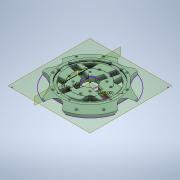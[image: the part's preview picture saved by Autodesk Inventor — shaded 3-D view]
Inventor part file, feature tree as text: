
AUTODESK INVENTOR PART (.ipt)
format: ipt  version: 2020 (Build 240168000, 168)  size: 684,032 bytes
history: native  units: mm
features: extrude x12, sketch x11, projected_geometry x8, other x6, pattern_circular x3, revolve x1, hole x1
ambient origin geometry x8: Origin, YZ Plane, XZ Plane, XY Plane, X Axis, Y Axis, Z Axis, Center Point
bodies: Body1 (feature_tree)
feature tree (42):
  other  "Твердое тело1"
  sketch  "Эскиз1"
  sketch  "Эскиз2"
  sketch  "Эскиз3"
  other  "РабОсь1"
  revolve  "Вращение1"
  hole  "Отверстие1"  [1 undecoded]
  other  "РабПлоскость1"
  other  "РабПлоскость2"
  extrude  "Выдавливание2"  Depth=44.0mm
  pattern_circular  "Круговой массив1"  Count=4 Angle=360.0deg
  other  "РабПлоскость3"
  extrude  "Выдавливание6"  Depth=7.0mm
  extrude  "Выдавливание7"  Depth=13.0mm
  pattern_circular  "Круговой массив2"  Angle=90.0deg  [1 undecoded]
  extrude  "Выдавливание8"  [1 undecoded]
  pattern_circular  "Круговой массив3"  [2 undecoded]
  extrude  "Выдавливание9"  Depth=6.0mm
  extrude  "Выдавливание10"  Depth=6.0mm
  other  "РабПлоскость4"
  extrude  "Выдавливание11"  Depth=6.0mm
  extrude  "Выдавливание1"  Depth=6.0mm
  extrude  "Выдавливание12"  Depth=6.0mm
  extrude  "Выдавливание13"  Depth=6.0mm
  extrude  "Выдавливание14"  Depth=6.0mm
  sketch  "Эскиз14"
  extrude  "Выдавливание15"  Depth=6.0mm
  sketch  "Эскиз5"
  sketch  "Эскиз9"
  sketch  "Эскиз10"
  sketch  "Эскиз11"
  sketch  "Эскиз12"
  sketch  "Эскиз13"
  projected_geometry  "Спроецированная петля1"
  projected_geometry  "Спроецированная петля2"
  projected_geometry  "Спроецированная петля3"
  projected_geometry  "Спроецированная петля4"
  projected_geometry  "Спроецированная петля5"
  projected_geometry  "Спроецированная петля6"
  projected_geometry  "Спроецированная петля7"
  projected_geometry  "Спроецированная петля8"
  sketch  "Эскиз15"
note: 5 required parameter values undecoded (feature->parameter linkage not recoverable at this tier; creation-order binding heuristic only, values carry confidence <= 0.55)
